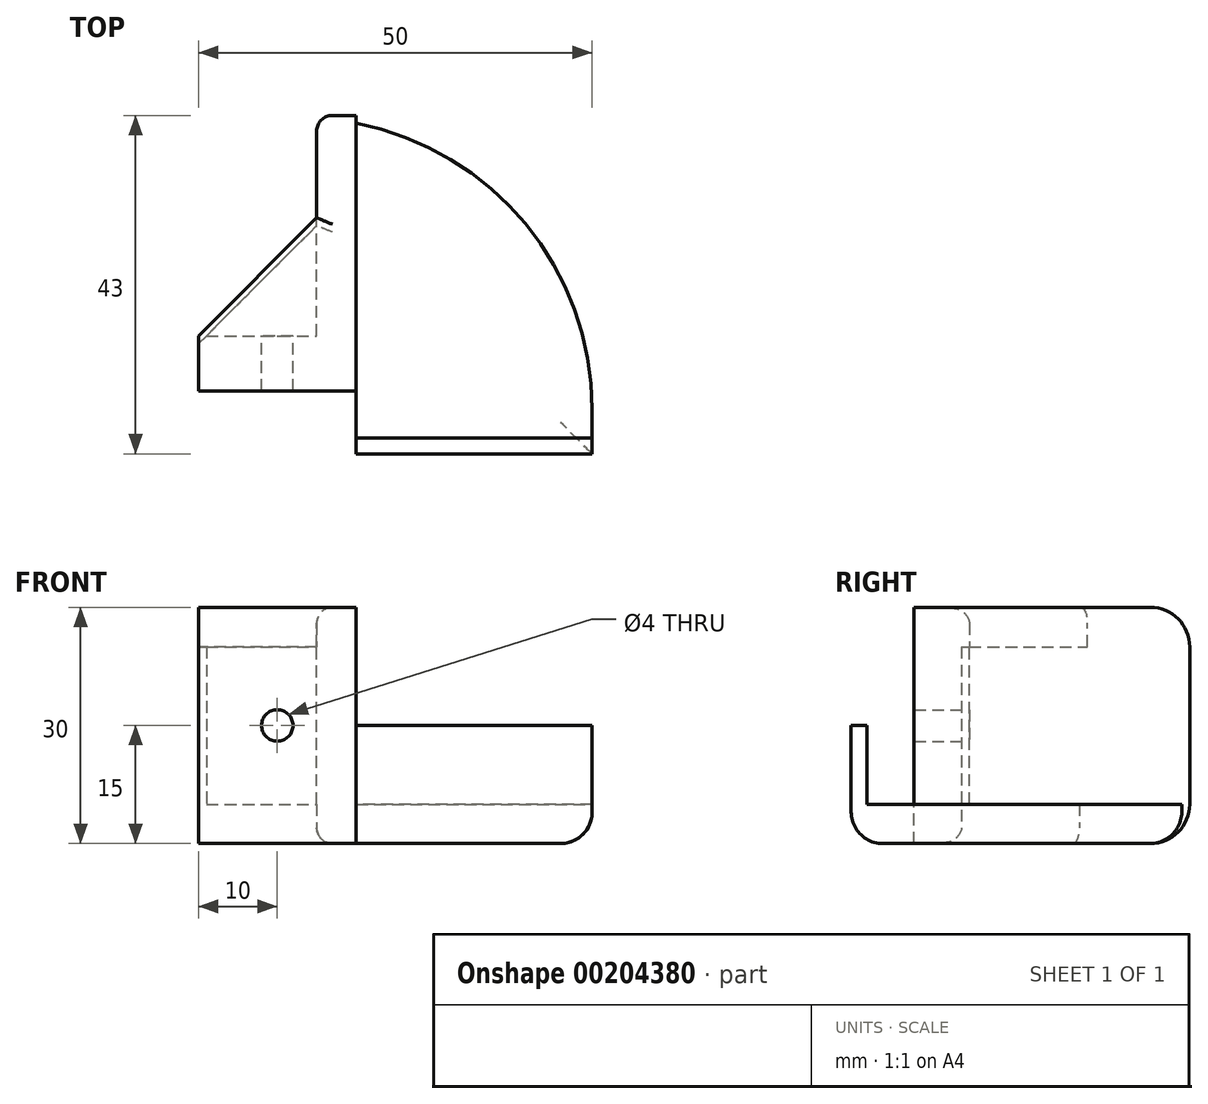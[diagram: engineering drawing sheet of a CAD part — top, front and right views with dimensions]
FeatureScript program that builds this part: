
annotation { "Feature Type Name" : "Feature", "Feature Type Description" : "" }
export const myFeature = defineFeature(function(context is Context, id is Id, definition is map)
    precondition{}
    {
        {
            var Q0;
            Q0=qCreatedBy(makeId("Top.planeOp"),FACE);
            var sketch = newSketch(context, id + "F0", { "sketchPlane" : qUnion([Q0])});
            skLineSegment(sketch, "E0.bottom", {"start": v(0, 0) * mm, "end": v(30, 0) * mm});
            skLineSegment(sketch, "E0.top", {"start": v(0, 42) * mm, "end": v(30, 42) * mm});
            skLineSegment(sketch, "E0.left", {"start": v(0, 0) * mm, "end": v(0, 42) * mm});
            skLineSegment(sketch, "E0.right", {"start": v(30, 0) * mm, "end": v(30, 42) * mm});
            skSolve(sketch);
        }
        {
            var Q0;
            Q0=makeQuery(id+"F0.imprint","IMPRINT",FACE,{"disambiguationData":[TD([[makeQuery(id+"F0.imprint","IMPRINT",EDGE,{"derivedFrom":sQuery(id+"F0.wireOp",EDGE,"E0.bottom")}),1.0]])]});
            extrude(context, id + "F1", {"entities" : qUnion([Q0]), "depth" : 5 * mm});
        }
        {
            var Q0;
            Q0=makeQuery(id+"F1.opExtrude","SWEPT_EDGE",EDGE,{"disambiguationData":[OSD([sQuery(id+"F0.wireOp",EDGE,"E0.top"),sQuery(id+"F0.wireOp",EDGE,"E0.right")])]});
            fillet(context, id + "F2", {"entities" : qUnion([Q0]), "radius" : 37 * mm, "tangentPropagation" : true, "allowEdgeOverflow" : false});
        }
        {
            var Q0;
            Q0=makeQuery(id+"F1.opExtrude","CAP_FACE",FACE,{"disambiguationData":[OSD([sQuery(id+"F0.wireOp",EDGE,"E0.bottom"),sQuery(id+"F0.wireOp",EDGE,"E0.top"),sQuery(id+"F0.wireOp",EDGE,"E0.left"),sQuery(id+"F0.wireOp",EDGE,"E0.right")])],"isStart":false});
            var sketch = newSketch(context, id + "F3", { "sketchPlane" : qUnion([Q0])});
            skLineSegment(sketch, "E1.bottom", {"start": v(0, 0) * mm, "end": v(30, 0) * mm});
            skLineSegment(sketch, "E1.top", {"start": v(0, 2) * mm, "end": v(30, 2) * mm});
            skLineSegment(sketch, "E1.left", {"start": v(0, 0) * mm, "end": v(0, 2) * mm});
            skLineSegment(sketch, "E1.right", {"start": v(30, 0) * mm, "end": v(30, 2) * mm});
            skSolve(sketch);
        }
        {
            var Q0;
            Q0 = qSketchRegion(id + "F3", true);
            extrude(context, id + "F4", {"entities" : qUnion([Q0]), "operationType" : NewBodyOperationType.ADD, "depth" : 10 * mm});
        }
        {
            var Q0;
            Q0=makeQuery(id+"F4.boolean.opBoolean","MERGE",FACE,{"derivedFrom":[makeQuery(id+"F1.opExtrude","SWEPT_FACE",FACE,{"disambiguationData":[OSD([sQuery(id+"F0.wireOp",EDGE,"E0.left")])]}),makeQuery(id+"F4.opExtrude","SWEPT_FACE",FACE,{"disambiguationData":[OSD([sQuery(id+"F3.wireOp",EDGE,"E1.left")])]})]});
            var sketch = newSketch(context, id + "F5", { "sketchPlane" : qUnion([Q0])});
            skLineSegment(sketch, "E2.bottom", {"start": v(-8, 0) * mm, "end": v(-43, 0) * mm});
            skLineSegment(sketch, "E2.top", {"start": v(-8, 30) * mm, "end": v(-43, 30) * mm});
            skLineSegment(sketch, "E2.left", {"start": v(-8, 0) * mm, "end": v(-8, 30) * mm});
            skLineSegment(sketch, "E2.right", {"start": v(-43, 0) * mm, "end": v(-43, 30) * mm});
            skSolve(sketch);
        }
        {
            var Q0;
            Q0 = qSketchRegion(id + "F5", true);
            extrude(context, id + "F6", {"entities" : qUnion([Q0]), "operationType" : NewBodyOperationType.ADD, "depth" : 5 * mm});
        }
        {
            var Q0;
            Q0=makeQuery(id+"F6.opExtrude","CAP_FACE",FACE,{"disambiguationData":[OSD([sQuery(id+"F5.wireOp",EDGE,"E2.bottom"),sQuery(id+"F5.wireOp",EDGE,"E2.top"),sQuery(id+"F5.wireOp",EDGE,"E2.left"),sQuery(id+"F5.wireOp",EDGE,"E2.right")])],"isStart":false});
            var sketch = newSketch(context, id + "F7", { "sketchPlane" : qUnion([Q0])});
            skLineSegment(sketch, "E3.bottom", {"start": v(-8, 0) * mm, "end": v(-8, 0) * mm});
            skLineSegment(sketch, "E3.top", {"start": v(-8, 30) * mm, "end": v(-8, 30) * mm});
            skLineSegment(sketch, "E3.left", {"start": v(-8, 0) * mm, "end": v(-8, 30) * mm});
            skLineSegment(sketch, "E3.right", {"start": v(-8, 0) * mm, "end": v(-8, 30) * mm});
            skLineSegment(sketch, "E4.bottom", {"start": v(-8, 0) * mm, "end": v(-15, 0) * mm});
            skLineSegment(sketch, "E4.top", {"start": v(-8, 30) * mm, "end": v(-15, 30) * mm});
            skLineSegment(sketch, "E4.right", {"start": v(-15, 0) * mm, "end": v(-15, 30) * mm});
            skSolve(sketch);
        }
        {
            var Q0;
            Q0 = qSketchRegion(id + "F7", true);
            extrude(context, id + "F8", {"entities" : qUnion([Q0]), "operationType" : NewBodyOperationType.ADD, "depth" : 15 * mm});
        }
        {
            var Q0;
            Q0=makeQuery(id+"F8.opExtrude","SWEPT_FACE",FACE,{"disambiguationData":[OSD([sQuery(id+"F7.wireOp",EDGE,"E4.right")])]});
            var sketch = newSketch(context, id + "F9", { "sketchPlane" : qUnion([Q0])});
            skCircle(sketch, "E5", {"center": v(10, 15) * mm, "radius": 2 * mm});
            skSolve(sketch);
        }
        {
            var Q0;
            Q0=makeQuery(id+"F9.imprint","IMPRINT",FACE,{"disambiguationData":[TD([[makeQuery(id+"F9.imprint","IMPRINT",EDGE,{"derivedFrom":sQuery(id+"F9.wireOp",EDGE,"E5")}),1.0]])]});
            var Q1;
            Q1=sQuery(id+"F9.wireOp",EDGE,"E5");
            extrude(context, id + "F10", {"entities" : qUnion([Q0]), "operationType" : NewBodyOperationType.REMOVE, "surfaceEntities" : qUnion([Q1]), "oppositeDirection" : true, "depth" : 10 * mm});
        }
        {
            var Q0;
            {var subQ0=sQuery(id+"F0.wireOp",EDGE,"E0.right");var subQ1=sQuery(id+"F0.wireOp",EDGE,"E0.top");Q0=makeQuery(id+"F2.opFillet","BLEND_EDGE",EDGE,{"blendedFrom":[makeQuery(id+"F1.opExtrude","SWEPT_EDGE",EDGE,{"disambiguationData":[OSD([subQ1,subQ0])]}),makeQuery(id+"F1.opExtrude","CAP_FACE",FACE,{"disambiguationData":[OSD([sQuery(id+"F0.wireOp",EDGE,"E0.bottom"),subQ1,sQuery(id+"F0.wireOp",EDGE,"E0.left"),subQ0])],"isStart":true})],"blendedInto":[makeQuery(id+"F1.opExtrude","CAP_FACE",FACE,{"disambiguationData":[OSD([sQuery(id+"F0.wireOp",EDGE,"E0.bottom"),subQ1,sQuery(id+"F0.wireOp",EDGE,"E0.left"),subQ0])],"isStart":true})]});}
            var Q1;
            Q1=makeQuery(id+"F1.opExtrude","CAP_EDGE",EDGE,{"disambiguationData":[OSD([sQuery(id+"F0.wireOp",EDGE,"E0.bottom")])],"isStart":true});
            fillet(context, id + "F11", {"entities" : qUnion([Q0, Q1]), "radius" : 4 * mm, "tangentPropagation" : true, "allowEdgeOverflow" : false});
        }
        {
            var Q0;
            Q0=makeQuery(id+"F8.boolean.opBoolean","MERGE",FACE,{"derivedFrom":[makeQuery(id+"F6.boolean.opBoolean","MERGE",FACE,{"derivedFrom":[makeQuery(id+"F1.opExtrude","CAP_FACE",FACE,{"disambiguationData":[OSD([sQuery(id+"F0.wireOp",EDGE,"E0.bottom"),sQuery(id+"F0.wireOp",EDGE,"E0.top"),sQuery(id+"F0.wireOp",EDGE,"E0.left"),sQuery(id+"F0.wireOp",EDGE,"E0.right")])],"isStart":true}),makeQuery(id+"F6.opExtrude","SWEPT_FACE",FACE,{"disambiguationData":[OSD([sQuery(id+"F5.wireOp",EDGE,"E2.bottom")])]})]}),makeQuery(id+"F8.opExtrude","SWEPT_FACE",FACE,{"disambiguationData":[OSD([sQuery(id+"F7.wireOp",EDGE,"E4.bottom")])]})]});
            var sketch = newSketch(context, id + "F12", { "sketchPlane" : qUnion([Q0])});
            skLineSegment(sketch, "E6.bottom", {"start": v(-20, -15) * mm, "end": v(-5, -15) * mm});
            skLineSegment(sketch, "E6.top", {"start": v(-20, -29) * mm, "end": v(-5, -29) * mm});
            skLineSegment(sketch, "E6.left", {"start": v(-20, -15) * mm, "end": v(-20, -29) * mm});
            skLineSegment(sketch, "E6.right", {"start": v(-5, -15) * mm, "end": v(-5, -29) * mm});
            skSolve(sketch);
        }
        {
            var Q0;
            Q0=makeQuery(id+"F12.imprint","IMPRINT",FACE,{"disambiguationData":[TD([[makeQuery(id+"F12.imprint","IMPRINT",EDGE,{"derivedFrom":sQuery(id+"F12.wireOp",EDGE,"E6.bottom")}),-1.0]])]});
            extrude(context, id + "F13", {"entities" : qUnion([Q0]), "operationType" : NewBodyOperationType.ADD, "oppositeDirection" : true, "depth" : 5 * mm});
        }
        {
            var Q0;
            Q0=makeQuery(id+"F8.boolean.opBoolean","MERGE",FACE,{"derivedFrom":[makeQuery(id+"F6.opExtrude","SWEPT_FACE",FACE,{"disambiguationData":[OSD([sQuery(id+"F5.wireOp",EDGE,"E2.top")])]}),makeQuery(id+"F8.opExtrude","SWEPT_FACE",FACE,{"disambiguationData":[OSD([sQuery(id+"F7.wireOp",EDGE,"E4.top")])]})]});
            var sketch = newSketch(context, id + "F14", { "sketchPlane" : qUnion([Q0])});
            skLineSegment(sketch, "E7.bottom", {"start": v(-5, 15) * mm, "end": v(-20, 15) * mm});
            skLineSegment(sketch, "E7.top", {"start": v(-5, 30) * mm, "end": v(-20, 30) * mm});
            skLineSegment(sketch, "E7.left", {"start": v(-5, 15) * mm, "end": v(-5, 30) * mm});
            skLineSegment(sketch, "E7.right", {"start": v(-20, 15) * mm, "end": v(-20, 30) * mm});
            skSolve(sketch);
        }
        {
            var Q0;
            Q0=makeQuery(id+"F14.imprint","IMPRINT",FACE,{"disambiguationData":[TD([[makeQuery(id+"F14.imprint","IMPRINT",EDGE,{"derivedFrom":sQuery(id+"F14.wireOp",EDGE,"E7.bottom")}),1.0]])]});
            extrude(context, id + "F15", {"entities" : qUnion([Q0]), "operationType" : NewBodyOperationType.ADD, "oppositeDirection" : true, "depth" : 5 * mm});
        }
        {
            var Q0;
            Q0=makeQuery(id+"F15.opExtrude","SWEPT_EDGE",EDGE,{"disambiguationData":[OSD([sQuery(id+"F14.wireOp",EDGE,"E7.top"),sQuery(id+"F14.wireOp",EDGE,"E7.right")])]});
            var Q1;
            Q1=makeQuery(id+"F13.opExtrude","SWEPT_EDGE",EDGE,{"disambiguationData":[OSD([sQuery(id+"F12.wireOp",EDGE,"E6.top"),sQuery(id+"F12.wireOp",EDGE,"E6.left")])]});
            chamfer(context, id + "F16", {"entities" : qUnion([Q0, Q1]), "width" : 15 * mm, "tangentPropagation" : true});
        }
        {
            var Q0;
            Q0=makeQuery(id+"F6.opExtrude","SWEPT_EDGE",EDGE,{"disambiguationData":[OSD([sQuery(id+"F5.wireOp",EDGE,"E2.bottom"),sQuery(id+"F5.wireOp",EDGE,"E2.right")])]});
            var Q1;
            Q1=makeQuery(id+"F6.opExtrude","SWEPT_EDGE",EDGE,{"disambiguationData":[OSD([sQuery(id+"F5.wireOp",EDGE,"E2.top"),sQuery(id+"F5.wireOp",EDGE,"E2.right")])]});
            fillet(context, id + "F17", {"entities" : qUnion([Q0, Q1]), "radius" : 5 * mm, "tangentPropagation" : true, "allowEdgeOverflow" : false});
        }
        {
            var Q0;
            Q0=makeQuery(id+"F6.opExtrude","CAP_EDGE",EDGE,{"disambiguationData":[OSD([sQuery(id+"F5.wireOp",EDGE,"E2.right")])],"isStart":false});
            var Q1;
            Q1=makeQuery(id+"F8.opExtrude","CAP_EDGE",EDGE,{"disambiguationData":[OSD([sQuery(id+"F7.wireOp",EDGE,"E4.right")])],"isStart":false});
            var Q2;
            {var subQ0=sQuery(id+"F12.wireOp",EDGE,"E6.left");var subQ1=sQuery(id+"F12.wireOp",EDGE,"E6.top");Q2=makeQuery(id+"F16.opChamfer","BLEND_EDGE",EDGE,{"blendedFrom":[makeQuery(id+"F13.opExtrude","SWEPT_EDGE",EDGE,{"disambiguationData":[OSD([subQ1,subQ0])]}),makeQuery(id+"F13.boolean.opBoolean","MERGE",FACE,{"derivedFrom":[makeQuery(id+"F8.boolean.opBoolean","MERGE",FACE,{"derivedFrom":[makeQuery(id+"F6.boolean.opBoolean","MERGE",FACE,{"derivedFrom":[makeQuery(id+"F1.opExtrude","CAP_FACE",FACE,{"disambiguationData":[OSD([sQuery(id+"F0.wireOp",EDGE,"E0.bottom"),sQuery(id+"F0.wireOp",EDGE,"E0.top"),sQuery(id+"F0.wireOp",EDGE,"E0.left"),sQuery(id+"F0.wireOp",EDGE,"E0.right")])],"isStart":true}),makeQuery(id+"F6.opExtrude","SWEPT_FACE",FACE,{"disambiguationData":[OSD([sQuery(id+"F5.wireOp",EDGE,"E2.bottom")])]})]}),makeQuery(id+"F8.opExtrude","SWEPT_FACE",FACE,{"disambiguationData":[OSD([sQuery(id+"F7.wireOp",EDGE,"E4.bottom")])]})]}),makeQuery(id+"F13.opExtrude","CAP_FACE",FACE,{"disambiguationData":[OSD([sQuery(id+"F12.wireOp",EDGE,"E6.bottom"),subQ1,subQ0,sQuery(id+"F12.wireOp",EDGE,"E6.right")])],"isStart":true})]})],"blendedInto":[makeQuery(id+"F13.boolean.opBoolean","MERGE",FACE,{"derivedFrom":[makeQuery(id+"F8.boolean.opBoolean","MERGE",FACE,{"derivedFrom":[makeQuery(id+"F6.boolean.opBoolean","MERGE",FACE,{"derivedFrom":[makeQuery(id+"F1.opExtrude","CAP_FACE",FACE,{"disambiguationData":[OSD([sQuery(id+"F0.wireOp",EDGE,"E0.bottom"),sQuery(id+"F0.wireOp",EDGE,"E0.top"),sQuery(id+"F0.wireOp",EDGE,"E0.left"),sQuery(id+"F0.wireOp",EDGE,"E0.right")])],"isStart":true}),makeQuery(id+"F6.opExtrude","SWEPT_FACE",FACE,{"disambiguationData":[OSD([sQuery(id+"F5.wireOp",EDGE,"E2.bottom")])]})]}),makeQuery(id+"F8.opExtrude","SWEPT_FACE",FACE,{"disambiguationData":[OSD([sQuery(id+"F7.wireOp",EDGE,"E4.bottom")])]})]}),makeQuery(id+"F13.opExtrude","CAP_FACE",FACE,{"disambiguationData":[OSD([sQuery(id+"F12.wireOp",EDGE,"E6.bottom"),subQ1,subQ0,sQuery(id+"F12.wireOp",EDGE,"E6.right")])],"isStart":true})]})]});}
            var Q3;
            {var subQ0=sQuery(id+"F14.wireOp",EDGE,"E7.right");var subQ1=sQuery(id+"F14.wireOp",EDGE,"E7.top");Q3=makeQuery(id+"F16.opChamfer","BLEND_EDGE",EDGE,{"blendedFrom":[makeQuery(id+"F15.opExtrude","SWEPT_EDGE",EDGE,{"disambiguationData":[OSD([subQ1,subQ0])]}),makeQuery(id+"F15.boolean.opBoolean","MERGE",FACE,{"derivedFrom":[makeQuery(id+"F8.boolean.opBoolean","MERGE",FACE,{"derivedFrom":[makeQuery(id+"F6.opExtrude","SWEPT_FACE",FACE,{"disambiguationData":[OSD([sQuery(id+"F5.wireOp",EDGE,"E2.top")])]}),makeQuery(id+"F8.opExtrude","SWEPT_FACE",FACE,{"disambiguationData":[OSD([sQuery(id+"F7.wireOp",EDGE,"E4.top")])]})]}),makeQuery(id+"F15.opExtrude","CAP_FACE",FACE,{"disambiguationData":[OSD([sQuery(id+"F14.wireOp",EDGE,"E7.bottom"),subQ1,sQuery(id+"F14.wireOp",EDGE,"E7.left"),subQ0])],"isStart":true})]})],"blendedInto":[makeQuery(id+"F15.boolean.opBoolean","MERGE",FACE,{"derivedFrom":[makeQuery(id+"F8.boolean.opBoolean","MERGE",FACE,{"derivedFrom":[makeQuery(id+"F6.opExtrude","SWEPT_FACE",FACE,{"disambiguationData":[OSD([sQuery(id+"F5.wireOp",EDGE,"E2.top")])]}),makeQuery(id+"F8.opExtrude","SWEPT_FACE",FACE,{"disambiguationData":[OSD([sQuery(id+"F7.wireOp",EDGE,"E4.top")])]})]}),makeQuery(id+"F15.opExtrude","CAP_FACE",FACE,{"disambiguationData":[OSD([sQuery(id+"F14.wireOp",EDGE,"E7.bottom"),subQ1,sQuery(id+"F14.wireOp",EDGE,"E7.left"),subQ0])],"isStart":true})]})]});}
            var Q4;
            Q4=makeQuery(id+"F6.opExtrude","CAP_EDGE",EDGE,{"disambiguationData":[OSD([sQuery(id+"F5.wireOp",EDGE,"E2.bottom")])],"isStart":false});
            var Q5;
            {var subQ0=sQuery(id+"F5.wireOp",EDGE,"E2.right");var subQ1=sQuery(id+"F5.wireOp",EDGE,"E2.bottom");Q5=makeQuery(id+"F17.opFillet","BLEND_EDGE",EDGE,{"blendedFrom":[makeQuery(id+"F6.opExtrude","SWEPT_EDGE",EDGE,{"disambiguationData":[OSD([subQ1,subQ0])]}),makeQuery(id+"F6.opExtrude","CAP_FACE",FACE,{"disambiguationData":[OSD([subQ1,sQuery(id+"F5.wireOp",EDGE,"E2.top"),sQuery(id+"F5.wireOp",EDGE,"E2.left"),subQ0])],"isStart":false})],"blendedInto":[makeQuery(id+"F6.opExtrude","CAP_FACE",FACE,{"disambiguationData":[OSD([subQ1,sQuery(id+"F5.wireOp",EDGE,"E2.top"),sQuery(id+"F5.wireOp",EDGE,"E2.left"),subQ0])],"isStart":false})]});}
            var Q6;
            {var subQ0=sQuery(id+"F5.wireOp",EDGE,"E2.right");var subQ1=sQuery(id+"F5.wireOp",EDGE,"E2.top");Q6=makeQuery(id+"F17.opFillet","BLEND_EDGE",EDGE,{"blendedFrom":[makeQuery(id+"F6.opExtrude","SWEPT_EDGE",EDGE,{"disambiguationData":[OSD([subQ1,subQ0])]}),makeQuery(id+"F6.opExtrude","CAP_FACE",FACE,{"disambiguationData":[OSD([sQuery(id+"F5.wireOp",EDGE,"E2.bottom"),subQ1,sQuery(id+"F5.wireOp",EDGE,"E2.left"),subQ0])],"isStart":false})],"blendedInto":[makeQuery(id+"F6.opExtrude","CAP_FACE",FACE,{"disambiguationData":[OSD([sQuery(id+"F5.wireOp",EDGE,"E2.bottom"),subQ1,sQuery(id+"F5.wireOp",EDGE,"E2.left"),subQ0])],"isStart":false})]});}
            var Q7;
            Q7=makeQuery(id+"F6.opExtrude","CAP_EDGE",EDGE,{"disambiguationData":[OSD([sQuery(id+"F5.wireOp",EDGE,"E2.top")])],"isStart":false});
            fillet(context, id + "F18", {"entities" : qUnion([Q0, Q1, Q2, Q3, Q4, Q5, Q6, Q7]), "radius" : 2 * mm, "tangentPropagation" : true, "allowEdgeOverflow" : false});
        }
    });
